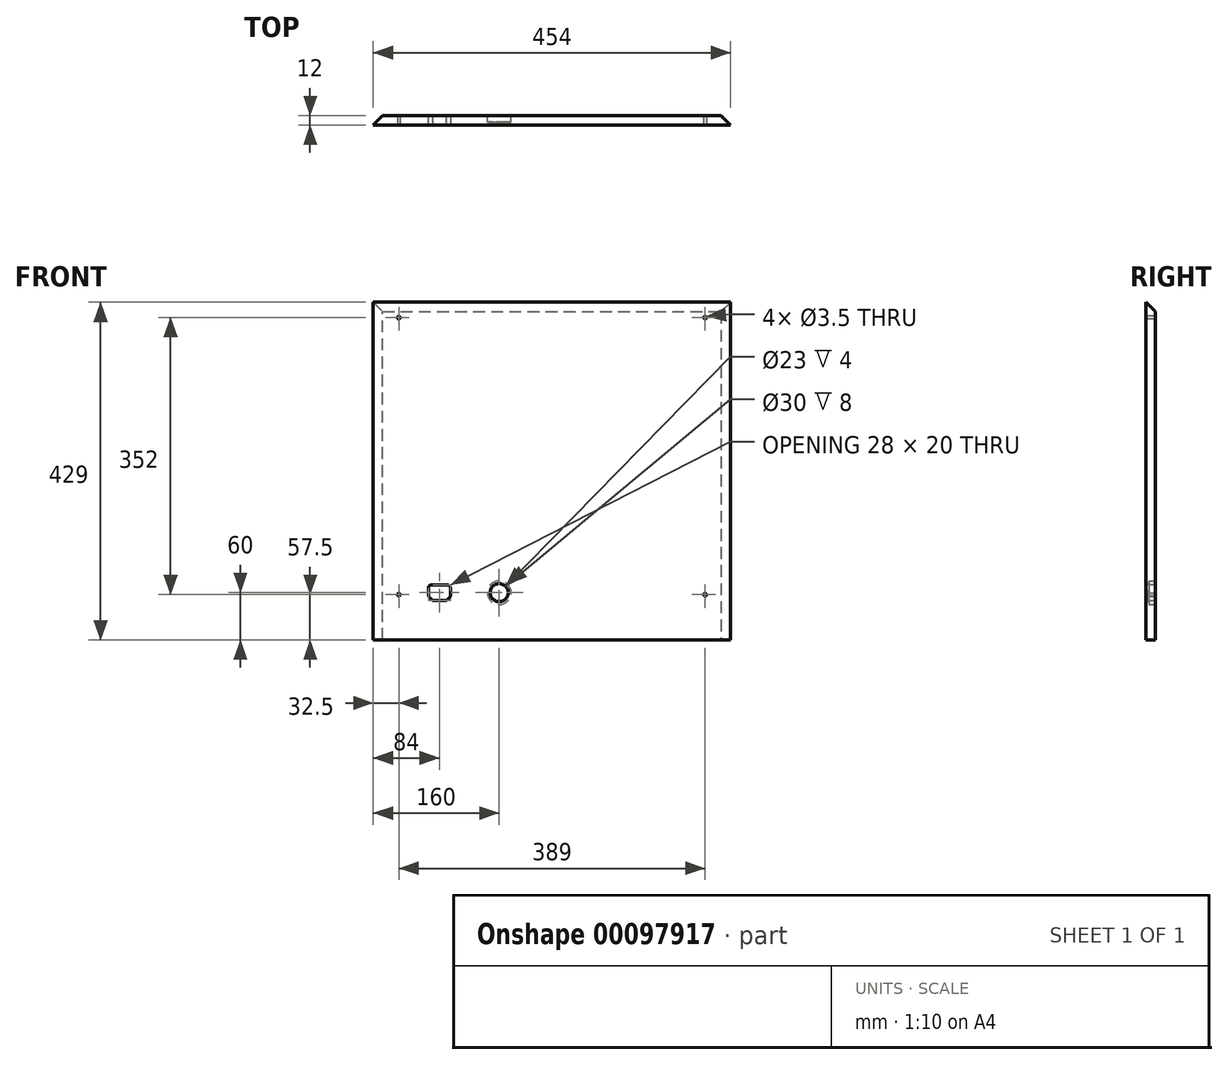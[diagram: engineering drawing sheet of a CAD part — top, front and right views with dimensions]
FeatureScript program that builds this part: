
annotation { "Feature Type Name" : "Feature", "Feature Type Description" : "" }
export const myFeature = defineFeature(function(context is Context, id is Id, definition is map)
    precondition{}
    {
        {
            var Q0;
            Q0=qCreatedBy(makeId("Front.planeOp"),FACE);
            var sketch = newSketch(context, id + "F0", { "sketchPlane" : qUnion([Q0])});
            skLineSegment(sketch, "E0.bottom", {"start": v(-227, 214.5) * mm, "end": v(227, 214.5) * mm});
            skLineSegment(sketch, "E0.top", {"start": v(-227, -214.5) * mm, "end": v(227, -214.5) * mm});
            skLineSegment(sketch, "E0.left", {"start": v(-227, 214.5) * mm, "end": v(-227, -214.5) * mm});
            skLineSegment(sketch, "E0.right", {"start": v(227, 214.5) * mm, "end": v(227, -214.5) * mm});
            skSolve(sketch);
        }
        {
            var Q0;
            Q0=makeQuery(id+"F0.imprint","IMPRINT",FACE,{"disambiguationData":[TD([[makeQuery(id+"F0.imprint","IMPRINT",EDGE,{"derivedFrom":sQuery(id+"F0.wireOp",EDGE,"E0.bottom")}),-1.0]])]});
            extrude(context, id + "F1", {"entities" : qUnion([Q0]), "depth" : 12 * mm});
        }
        {
            var Q0;
            Q0=makeQuery(id+"F1.opExtrude","CAP_EDGE",EDGE,{"disambiguationData":[OSD([sQuery(id+"F0.wireOp",EDGE,"E0.right")])],"isStart":true});
            var Q1;
            Q1=makeQuery(id+"F1.opExtrude","CAP_EDGE",EDGE,{"disambiguationData":[OSD([sQuery(id+"F0.wireOp",EDGE,"E0.left")])],"isStart":true});
            var Q2;
            Q2=makeQuery(id+"F1.opExtrude","CAP_EDGE",EDGE,{"disambiguationData":[OSD([sQuery(id+"F0.wireOp",EDGE,"E0.bottom")])],"isStart":true});
            chamfer(context, id + "F2", {"entities" : qUnion([Q0, Q1, Q2]), "width" : 12 * mm, "tangentPropagation" : true});
        }
        {
            var Q0;
            Q0=makeQuery(id+"F1.opExtrude","CAP_FACE",FACE,{"disambiguationData":[OSD([sQuery(id+"F0.wireOp",EDGE,"E0.bottom"),sQuery(id+"F0.wireOp",EDGE,"E0.top"),sQuery(id+"F0.wireOp",EDGE,"E0.left"),sQuery(id+"F0.wireOp",EDGE,"E0.right")])],"isStart":false});
            var sketch = newSketch(context, id + "F3", { "sketchPlane" : qUnion([Q0])});
            skCircle(sketch, "E1", {"center": v(-67, -154.5) * mm, "radius": 11.5 * mm});
            skLineSegment(sketch, "E2", {"start": v(-157, -144.5) * mm, "end": v(-129, -144.5) * mm});
            skLineSegment(sketch, "E3", {"start": v(-129, -144.5) * mm, "end": v(-129, -164.5) * mm});
            skLineSegment(sketch, "E4", {"start": v(-129, -164.5) * mm, "end": v(-157, -164.5) * mm});
            skLineSegment(sketch, "E5", {"start": v(-157, -164.5) * mm, "end": v(-157, -144.5) * mm});
            skSolve(sketch);
        }
        {
            var Q0;
            Q0=makeQuery(id+"F3.imprint","IMPRINT",FACE,{"disambiguationData":[TD([[makeQuery(id+"F3.imprint","IMPRINT",EDGE,{"derivedFrom":sQuery(id+"F3.wireOp",EDGE,"E2")}),-1.0]])]});
            var Q1;
            Q1=makeQuery(id+"F3.imprint","IMPRINT",FACE,{"disambiguationData":[TD([[makeQuery(id+"F3.imprint","IMPRINT",EDGE,{"derivedFrom":sQuery(id+"F3.wireOp",EDGE,"E1")}),1.0]])]});
            extrude(context, id + "F4", {"entities" : qUnion([Q0, Q1]), "operationType" : NewBodyOperationType.REMOVE, "oppositeDirection" : true, "depth" : 25 * mm});
        }
        {
            var Q0;
            Q0=makeQuery(id+"F4.boolean.opBoolean","COPY",EDGE,{"derivedFrom":makeQuery(id+"F4.opExtrude","SWEPT_EDGE",EDGE,{"disambiguationData":[OSD([sQuery(id+"F3.wireOp",EDGE,"E2"),sQuery(id+"F3.wireOp",EDGE,"E3")])]})});
            var Q1;
            Q1=makeQuery(id+"F4.boolean.opBoolean","COPY",EDGE,{"derivedFrom":makeQuery(id+"F4.opExtrude","SWEPT_EDGE",EDGE,{"disambiguationData":[OSD([sQuery(id+"F3.wireOp",EDGE,"E2"),sQuery(id+"F3.wireOp",EDGE,"E5")])]})});
            fillet(context, id + "F5", {"entities" : qUnion([Q0, Q1]), "radius" : 4 * mm, "tangentPropagation" : true, "allowEdgeOverflow" : false});
        }
        {
            var Q0;
            Q0=makeQuery(id+"F4.boolean.opBoolean","COPY",EDGE,{"derivedFrom":makeQuery(id+"F4.opExtrude","SWEPT_EDGE",EDGE,{"disambiguationData":[OSD([sQuery(id+"F3.wireOp",EDGE,"E4"),sQuery(id+"F3.wireOp",EDGE,"E5")])]})});
            var Q1;
            Q1=makeQuery(id+"F4.boolean.opBoolean","COPY",EDGE,{"derivedFrom":makeQuery(id+"F4.opExtrude","SWEPT_EDGE",EDGE,{"disambiguationData":[OSD([sQuery(id+"F3.wireOp",EDGE,"E3"),sQuery(id+"F3.wireOp",EDGE,"E4")])]})});
            chamfer(context, id + "F6", {"entities" : qUnion([Q0, Q1]), "width" : 5 * mm, "tangentPropagation" : true});
        }
        {
            var Q0;
            Q0=makeQuery(id+"F1.opExtrude","CAP_FACE",FACE,{"disambiguationData":[OSD([sQuery(id+"F0.wireOp",EDGE,"E0.bottom"),sQuery(id+"F0.wireOp",EDGE,"E0.top"),sQuery(id+"F0.wireOp",EDGE,"E0.left"),sQuery(id+"F0.wireOp",EDGE,"E0.right")])],"isStart":false});
            var sketch = newSketch(context, id + "F7", { "sketchPlane" : qUnion([Q0])});
            skLineSegment(sketch, "E6.0", {"start": v(-207.5, 195) * mm, "end": v(-207.5, -195) * mm, "construction": true});
            skLineSegment(sketch, "E6.1", {"start": v(207.5, 195) * mm, "end": v(-207.5, 195) * mm, "construction": true});
            skLineSegment(sketch, "E6.2", {"start": v(207.5, -195) * mm, "end": v(207.5, 195) * mm, "construction": true});
            skLineSegment(sketch, "E6.3", {"start": v(-207.5, -195) * mm, "end": v(207.5, -195) * mm, "construction": true});
            skLineSegment(sketch, "E7.0", {"start": v(-194.5, 182) * mm, "end": v(-194.5, -182) * mm, "construction": true});
            skLineSegment(sketch, "E7.1", {"start": v(194.5, 182) * mm, "end": v(-194.5, 182) * mm, "construction": true});
            skLineSegment(sketch, "E7.2", {"start": v(194.5, -182) * mm, "end": v(194.5, 182) * mm, "construction": true});
            skLineSegment(sketch, "E7.3", {"start": v(-194.5, -182) * mm, "end": v(194.5, -182) * mm, "construction": true});
            skLineSegment(sketch, "E8", {"start": v(-194.5, -157) * mm, "end": v(194.5, -157) * mm, "construction": true});
            skPoint(sketch, "E9", {"position": v(-194.5, 195) * mm});
            skPoint(sketch, "E10", {"position": v(194.5, 195) * mm});
            skSolve(sketch);
        }
        {
            var Q0;
            Q0=sQuery(id+"F7.wireOp",VERTEX,"E9");
            var Q1;
            Q1=sQuery(id+"F7.wireOp",VERTEX,"E10");
            var Q2;
            Q2=sQuery(id+"F7.wireOp",VERTEX,"E8.end");
            var Q3;
            Q3=sQuery(id+"F7.wireOp",VERTEX,"E8.start");
            var Q4;
            Q4=makeQuery(id+"F1.opExtrude","SWEPT_BODY",BODY,{"disambiguationData":[OSD([sQuery(id+"F0.wireOp",EDGE,"E0.bottom"),sQuery(id+"F0.wireOp",EDGE,"E0.top"),sQuery(id+"F0.wireOp",EDGE,"E0.left"),sQuery(id+"F0.wireOp",EDGE,"E0.right")])]});
            hole(context, id + "F8", {"style" : HoleStyle.SIMPLE, "endStyle" : HoleEndStyle.THROUGH, "holeDiameter" : 3.5 * mm, "locations" : qUnion([Q0, Q1, Q2, Q3]), "scope" : qUnion([Q4]), "isTappedThrough" : true});
        }
        {
            var Q0;
            Q0=makeQuery(id+"F1.opExtrude","CAP_FACE",FACE,{"disambiguationData":[OSD([sQuery(id+"F0.wireOp",EDGE,"E0.bottom"),sQuery(id+"F0.wireOp",EDGE,"E0.top"),sQuery(id+"F0.wireOp",EDGE,"E0.left"),sQuery(id+"F0.wireOp",EDGE,"E0.right")])],"isStart":true});
            var sketch = newSketch(context, id + "F9", { "sketchPlane" : qUnion([Q0])});
            skCircle(sketch, "E11.0", {"center": v(67, -154.5) * mm, "radius": 11.5 * mm});
            skCircle(sketch, "E12", {"center": v(67, -154.5) * mm, "radius": 15 * mm});
            skSolve(sketch);
        }
        {
            var Q0;
            Q0=makeQuery(id+"F9.imprint","IMPRINT",FACE,{"disambiguationData":[TD([[makeQuery(id+"F9.imprint","IMPRINT",EDGE,{"derivedFrom":sQuery(id+"F9.wireOp",EDGE,"E11.0")}),1.0]])]});
            extrude(context, id + "F10", {"entities" : qUnion([Q0]), "operationType" : NewBodyOperationType.REMOVE, "oppositeDirection" : true, "depth" : 8 * mm});
        }
    });
